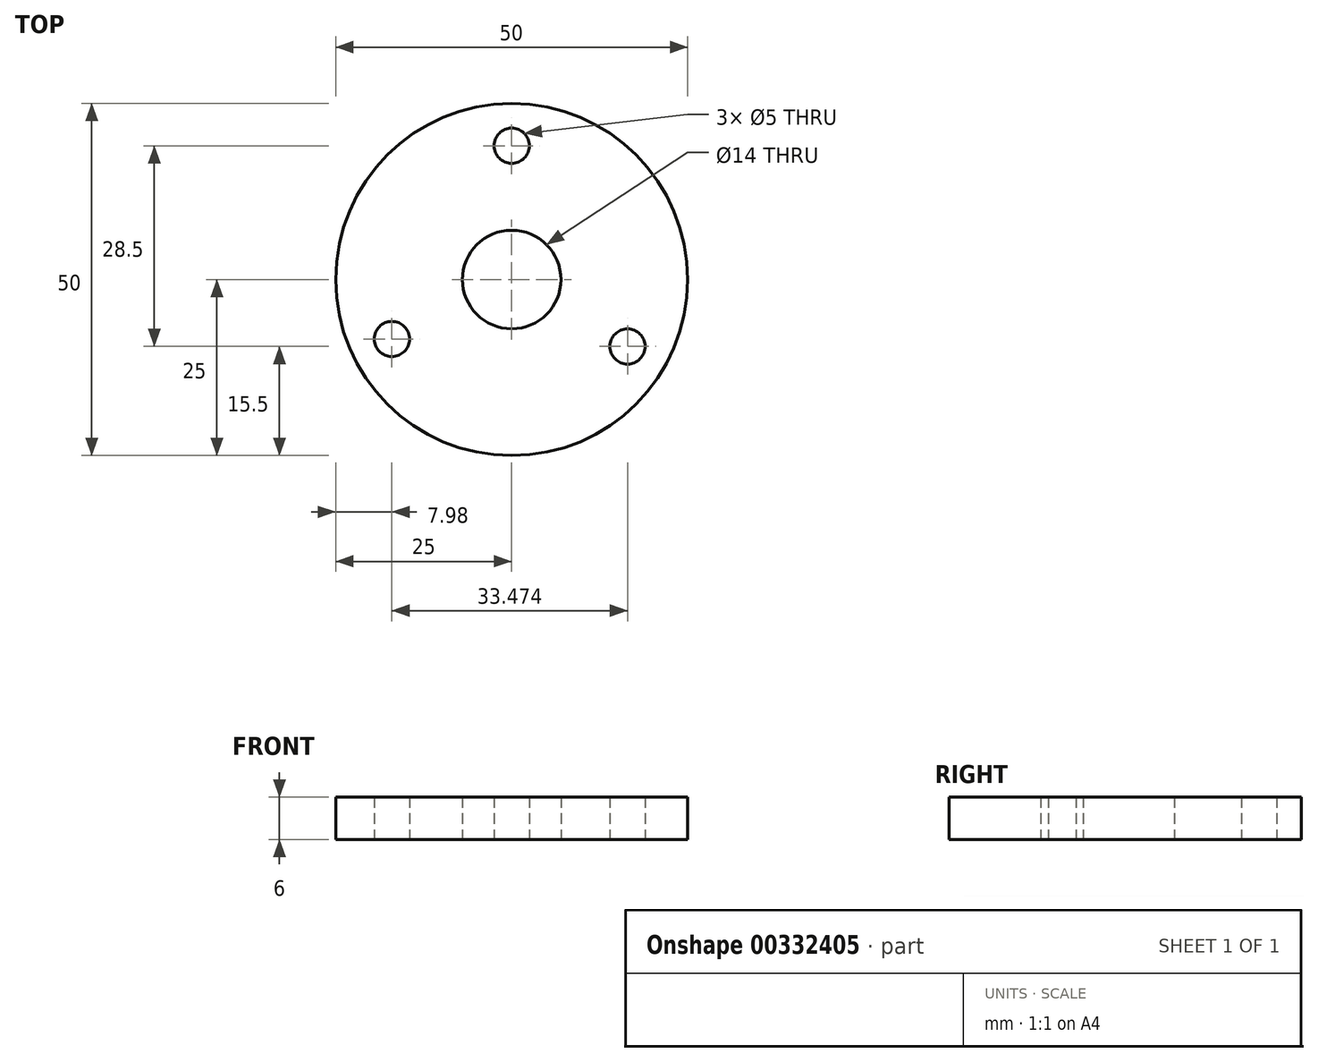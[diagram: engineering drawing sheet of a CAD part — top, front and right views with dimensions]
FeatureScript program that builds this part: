
annotation { "Feature Type Name" : "Feature", "Feature Type Description" : "" }
export const myFeature = defineFeature(function(context is Context, id is Id, definition is map)
    precondition{}
    {
        {
            var Q0;
            Q0=qCreatedBy(makeId("Top.planeOp"),FACE);
            var sketch = newSketch(context, id + "F0", { "sketchPlane" : qUnion([Q0])});
            skCircle(sketch, "E0", {"center": v(0, 0) * mm, "radius": 25 * mm});
            skCircle(sketch, "E1", {"center": v(0, 19) * mm, "radius": 2.5 * mm});
            skCircle(sketch, "E2", {"center": v(0, 0) * mm, "radius": 7 * mm});
            skCircle(sketch, "E3", {"center": v(16.45, -9.5) * mm, "radius": 2.5 * mm});
            skCircle(sketch, "E4", {"center": v(-17.02, -8.45) * mm, "radius": 2.5 * mm});
            skLineSegment(sketch, "E5.trimOffspring", {"start": v(-14.78, -7.33) * mm, "end": v(-17.02, -8.45) * mm});
            skSolve(sketch);
        }
        {
            var Q0;
            Q0=makeQuery(id+"F0.imprint","IMPRINT",FACE,{"disambiguationData":[TD([[makeQuery(id+"F0.imprint","IMPRINT",EDGE,{"derivedFrom":sQuery(id+"F0.wireOp",EDGE,"E0")}),1.0]])]});
            extrude(context, id + "F1", {"entities" : qUnion([Q0]), "depth" : 6 * mm});
        }
    });
